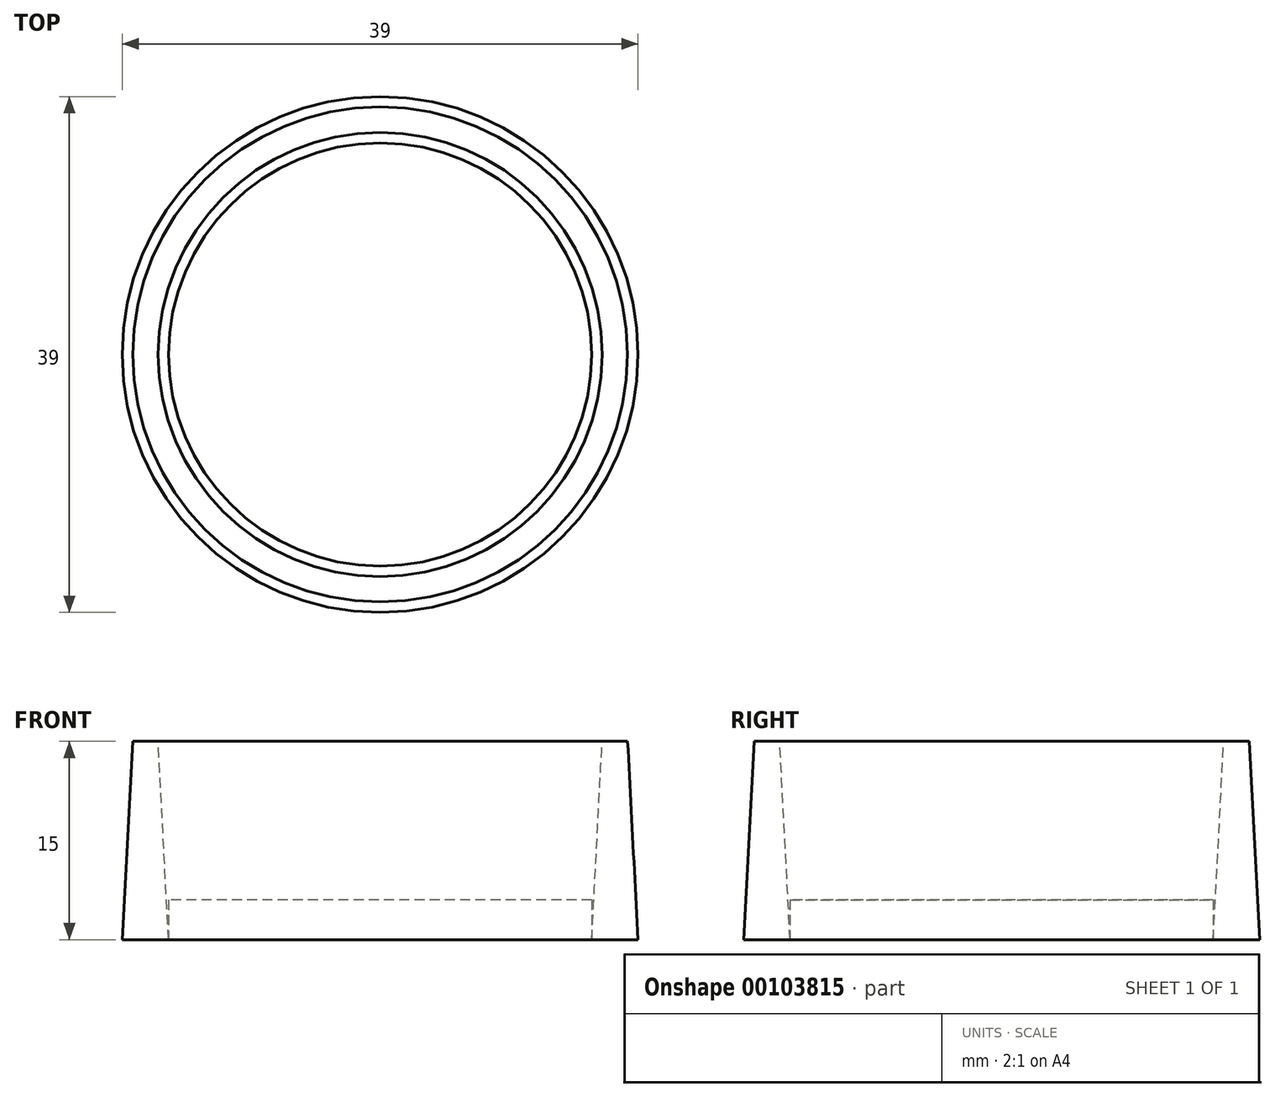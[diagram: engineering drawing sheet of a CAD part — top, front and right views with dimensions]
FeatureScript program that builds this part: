
annotation { "Feature Type Name" : "Feature", "Feature Type Description" : "" }
export const myFeature = defineFeature(function(context is Context, id is Id, definition is map)
    precondition{}
    {
        {
            var Q0;
            Q0=qCreatedBy(makeId("Top.planeOp"),FACE);
            var sketch = newSketch(context, id + "F0", { "sketchPlane" : qUnion([Q0])});
            skCircle(sketch, "E0", {"center": v(0, 0) * mm, "radius": 19.5 * mm});
            skCircle(sketch, "E1.0", {"center": v(0, 0) * mm, "radius": 16 * mm});
            skSolve(sketch);
        }
        {
            var Q0;
            Q0=makeQuery(id+"F0.imprint","IMPRINT",FACE,{"disambiguationData":[TD([[makeQuery(id+"F0.imprint","IMPRINT",EDGE,{"derivedFrom":sQuery(id+"F0.wireOp",EDGE,"E0")}),1.0]])]});
            extrude(context, id + "F1", {"entities" : qUnion([Q0]), "depth" : 15 * mm, "hasDraft" : true, "draftAngle" : 3 * degree, "draftPullDirection" : true});
        }
        {
            var Q0;
            Q0=makeQuery(id+"F0.imprint","IMPRINT",FACE,{"disambiguationData":[TD([[makeQuery(id+"F0.imprint","IMPRINT",EDGE,{"derivedFrom":sQuery(id+"F0.wireOp",EDGE,"E1.0")}),1.0]])]});
            extrude(context, id + "F2", {"entities" : qUnion([Q0]), "operationType" : NewBodyOperationType.ADD, "depth" : 3 * mm});
        }
    });
